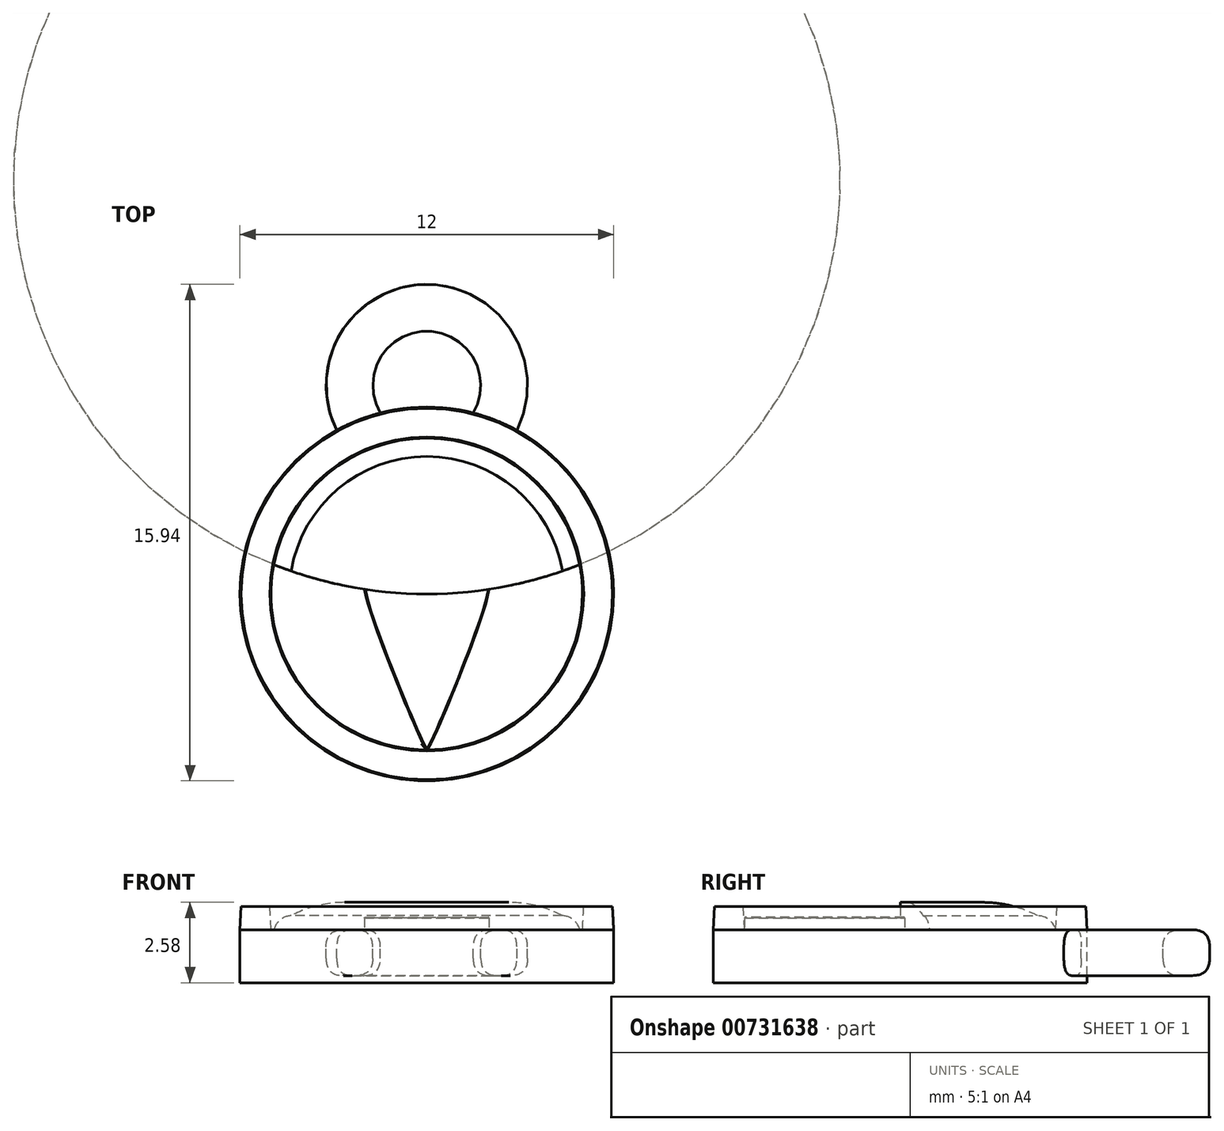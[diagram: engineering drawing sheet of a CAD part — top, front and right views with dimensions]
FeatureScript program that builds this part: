
annotation { "Feature Type Name" : "Feature", "Feature Type Description" : "" }
export const myFeature = defineFeature(function(context is Context, id is Id, definition is map)
    precondition{}
    {
        {
            var Q0;
            Q0=qCreatedBy(makeId("Top.planeOp"),FACE);
            var sketch = newSketch(context, id + "F0", { "sketchPlane" : qUnion([Q0])});
            skCircle(sketch, "E0", {"center": v(0, 0) * mm, "radius": 5 * mm});
            skArc(sketch, "E1", {"start": v(-4.91, 0.94) * mm, "mid": v(0, 0) * mm, "end": v(4.91, 0.94) * mm});
            skFitSpline(sketch, "E2", {"points": [v(-2, 0.15) * mm, v(-0.11, -4.83) * mm, v(0, -5) * mm, v(0.12, -4.83) * mm, v(2, 0.15) * mm], "startDerivative": vector(1.4, -7.6) * mm, "endDerivative": vector(1.32, 7.6) * mm});
            skCircle(sketch, "E3", {"center": v(0, 0) * mm, "radius": 6 * mm});
            skSolve(sketch);
        }
        {
            var Q0;
            Q0 = qSketchRegion(id + "F0", true);
            var Q1;
            {var subQ0=sQuery(id+"F0.wireOp",EDGE,"E2");var subQ1=sQuery(id+"F0.wireOp",EDGE,"E1");var subQ2=makeQuery(id+"F0.imprint","INTERSECT",VERTEX,{"disambiguationData":[OD(0.0)],"derivedFrom":[subQ1,subQ0]});Q1=makeQuery(id+"F0.imprint","IMPRINT",FACE,{"disambiguationData":[TD([[makeQuery(id+"F0.imprint","IMPRINT",EDGE,{"disambiguationData":[TD([[subQ2,-1.0]])],"derivedFrom":subQ1}),-1.0]])]});}
            var Q2;
            {var subQ0=sQuery(id+"F0.wireOp",EDGE,"E1");var subQ1=sQuery(id+"F0.wireOp",EDGE,"E0");var subQ2=makeQuery(id+"F0.imprint","INTERSECT",VERTEX,{"disambiguationData":[OD(0.0)],"derivedFrom":[subQ1,subQ0]});Q2=makeQuery(id+"F0.imprint","IMPRINT",FACE,{"disambiguationData":[TD([[makeQuery(id+"F0.imprint","IMPRINT",EDGE,{"disambiguationData":[TD([[subQ2,-1.0]])],"derivedFrom":subQ1}),1.0]])]});}
            var Q3;
            {var subQ0=sQuery(id+"F0.wireOp",EDGE,"E1");var subQ1=sQuery(id+"F0.wireOp",EDGE,"E0");var subQ2=makeQuery(id+"F0.imprint","INTERSECT",VERTEX,{"disambiguationData":[OD(1.0)],"derivedFrom":[subQ1,subQ0]});Q3=makeQuery(id+"F0.imprint","IMPRINT",FACE,{"disambiguationData":[TD([[makeQuery(id+"F0.imprint","IMPRINT",EDGE,{"disambiguationData":[TD([[subQ2,1.0]])],"derivedFrom":subQ1}),1.0]])]});}
            var Q4;
            {var subQ0=sQuery(id+"F0.wireOp",EDGE,"E1");var subQ1=sQuery(id+"F0.wireOp",EDGE,"E0");var subQ2=makeQuery(id+"F0.imprint","INTERSECT",VERTEX,{"disambiguationData":[OD(0.0)],"derivedFrom":[subQ1,subQ0]});Q4=makeQuery(id+"F0.imprint","IMPRINT",FACE,{"disambiguationData":[TD([[makeQuery(id+"F0.imprint","IMPRINT",EDGE,{"disambiguationData":[TD([[subQ2,1.0]])],"derivedFrom":subQ1}),1.0]])]});}
            extrude(context, id + "F1", {"entities" : qUnion([Q0, Q1, Q2, Q3, Q4]), "oppositeDirection" : true, "depth" : 1.7 * mm, "offsetDistance" : 25 * mm});
        }
        {
            var Q0;
            {var subQ0=sQuery(id+"F0.wireOp",EDGE,"E2");var subQ1=sQuery(id+"F0.wireOp",EDGE,"E1");var subQ2=makeQuery(id+"F0.imprint","INTERSECT",VERTEX,{"disambiguationData":[OD(0.0)],"derivedFrom":[subQ1,subQ0]});Q0=makeQuery(id+"F0.imprint","IMPRINT",FACE,{"disambiguationData":[TD([[makeQuery(id+"F0.imprint","IMPRINT",EDGE,{"disambiguationData":[TD([[subQ2,-1.0]])],"derivedFrom":subQ1}),-1.0]])]});}
            var Q1;
            Q1=makeQuery(id+"F4.opExtrude","CAP_FACE",FACE,{"disambiguationData":[OSD([sQuery(id+"F0.wireOp",EDGE,"E0"),sQuery(id+"F0.wireOp",EDGE,"E1")])],"isStart":false});
            extrude(context, id + "F2", {"entities" : qUnion([Q0]), "operationType" : NewBodyOperationType.ADD, "depth" : 0.4 * mm, "endBoundEntityFace" : qUnion([Q1]), "offsetDistance" : 25 * mm});
        }
        {
            var Q0;
            Q0=makeQuery(id+"F2.opExtrude","CAP_FACE",FACE,{"disambiguationData":[OSD([sQuery(id+"F0.wireOp",EDGE,"E1"),sQuery(id+"F0.wireOp",EDGE,"E2")])],"isStart":false});
            fillet(context, id + "F3", {"entities" : qUnion([Q0]), "radius" : 0.02 * mm, "tangentPropagation" : true, "allowEdgeOverflow" : false});
        }
        {
            var Q0;
            {var subQ0=sQuery(id+"F0.wireOp",EDGE,"E1");var subQ1=sQuery(id+"F0.wireOp",EDGE,"E0");var subQ2=makeQuery(id+"F0.imprint","INTERSECT",VERTEX,{"disambiguationData":[OD(0.0)],"derivedFrom":[subQ1,subQ0]});Q0=makeQuery(id+"F0.imprint","IMPRINT",FACE,{"disambiguationData":[TD([[makeQuery(id+"F0.imprint","IMPRINT",EDGE,{"disambiguationData":[TD([[subQ2,1.0]])],"derivedFrom":subQ1}),1.0]])]});}
            extrude(context, id + "F4", {"entities" : qUnion([Q0]), "operationType" : NewBodyOperationType.ADD, "depth" : 0.45 * mm, "offsetDistance" : 25 * mm});
        }
        {
            var Q0;
            Q0=makeQuery(id+"F4.opExtrude","CAP_EDGE",EDGE,{"disambiguationData":[OSD([sQuery(id+"F0.wireOp",EDGE,"E0")])],"isStart":false});
            fillet(context, id + "F5", {"entities" : qUnion([Q0]), "radius" : 0.6 * mm, "tangentPropagation" : true, "allowEdgeOverflow" : false});
        }
        {
            var Q0;
            Q0=qCreatedBy(makeId("Top.planeOp"),FACE);
            var sketch = newSketch(context, id + "F6", { "sketchPlane" : qUnion([Q0])});
            skArc(sketch, "E4", {"start": v(0.81, 5.17) * mm, "mid": v(0, 8.44) * mm, "end": v(-0.81, 5.17) * mm});
            skArc(sketch, "E5", {"start": v(2.85, 5.17) * mm, "mid": v(0, 9.94) * mm, "end": v(-2.85, 5.17) * mm});
            skLineSegment(sketch, "E6", {"start": v(-2.85, 5.17) * mm, "end": v(2.85, 5.17) * mm});
            skSolve(sketch);
        }
        {
            var Q0;
            {var subQ0=sQuery(id+"F6.wireOp",EDGE,"E4");Q0=makeQuery(id+"F6.imprint","IMPRINT",FACE,{"disambiguationData":[TD([[makeQuery(id+"F6.imprint","IMPRINT",EDGE,{"derivedFrom":subQ0}),-1.0]])]});}
            extrude(context, id + "F7", {"entities" : qUnion([Q0]), "operationType" : NewBodyOperationType.ADD, "oppositeDirection" : true, "depth" : 1.47 * mm, "offsetDistance" : 25 * mm});
        }
        {
            var Q0;
            Q0=makeQuery(id+"F7.opExtrude","CAP_EDGE",EDGE,{"disambiguationData":[OSD([sQuery(id+"F6.wireOp",EDGE,"E4")])],"isStart":true});
            var Q1;
            Q1=makeQuery(id+"F7.opExtrude","CAP_EDGE",EDGE,{"disambiguationData":[OSD([sQuery(id+"F6.wireOp",EDGE,"E5")])],"isStart":true});
            var Q2;
            Q2=makeQuery(id+"F7.opExtrude","CAP_EDGE",EDGE,{"disambiguationData":[OSD([sQuery(id+"F6.wireOp",EDGE,"E4")])],"isStart":false});
            var Q3;
            Q3=makeQuery(id+"F7.opExtrude","CAP_EDGE",EDGE,{"disambiguationData":[OSD([sQuery(id+"F6.wireOp",EDGE,"E5")])],"isStart":false});
            fillet(context, id + "F8", {"entities" : qUnion([Q0, Q1, Q2, Q3]), "radius" : 0.56 * mm, "tangentPropagation" : true, "rho" : 0.5, "crossSection" : FilletCrossSection.CONIC, "allowEdgeOverflow" : false});
        }
        {
            var Q0;
            Q0=makeQuery(id+"F4.opExtrude","CAP_FACE",FACE,{"disambiguationData":[OSD([sQuery(id+"F0.wireOp",EDGE,"E0"),sQuery(id+"F0.wireOp",EDGE,"E1")])],"isStart":false});
            extrude(context, id + "F9", {"entities" : qUnion([Q0]), "operationType" : NewBodyOperationType.ADD, "depth" : 0.43 * mm, "offsetDistance" : 25 * mm});
        }
        {
            var Q0;
            Q0=makeQuery(id+"F9.opExtrude","CAP_EDGE",EDGE,{"disambiguationData":[OSD([sQuery(id+"F0.wireOp",EDGE,"E0"),sQuery(id+"F0.wireOp",EDGE,"E1")])],"isStart":false});
            fillet(context, id + "F10", {"entities" : qUnion([Q0]), "radius" : 3.84 * mm, "tangentPropagation" : true, "allowEdgeOverflow" : false});
        }
        {
            var Q0;
            Q0=makeQuery(id+"F0.imprint","IMPRINT",FACE,{"disambiguationData":[TD([[makeQuery(id+"F0.imprint","IMPRINT",EDGE,{"derivedFrom":sQuery(id+"F0.wireOp",EDGE,"E3")}),1.0]])]});
            extrude(context, id + "F11", {"entities" : qUnion([Q0]), "operationType" : NewBodyOperationType.ADD, "depth" : 0.75 * mm, "offsetDistance" : 25 * mm, "hasDraft" : true, "draftAngle" : 3 * degree, "draftPullDirection" : true});
        }
    });
